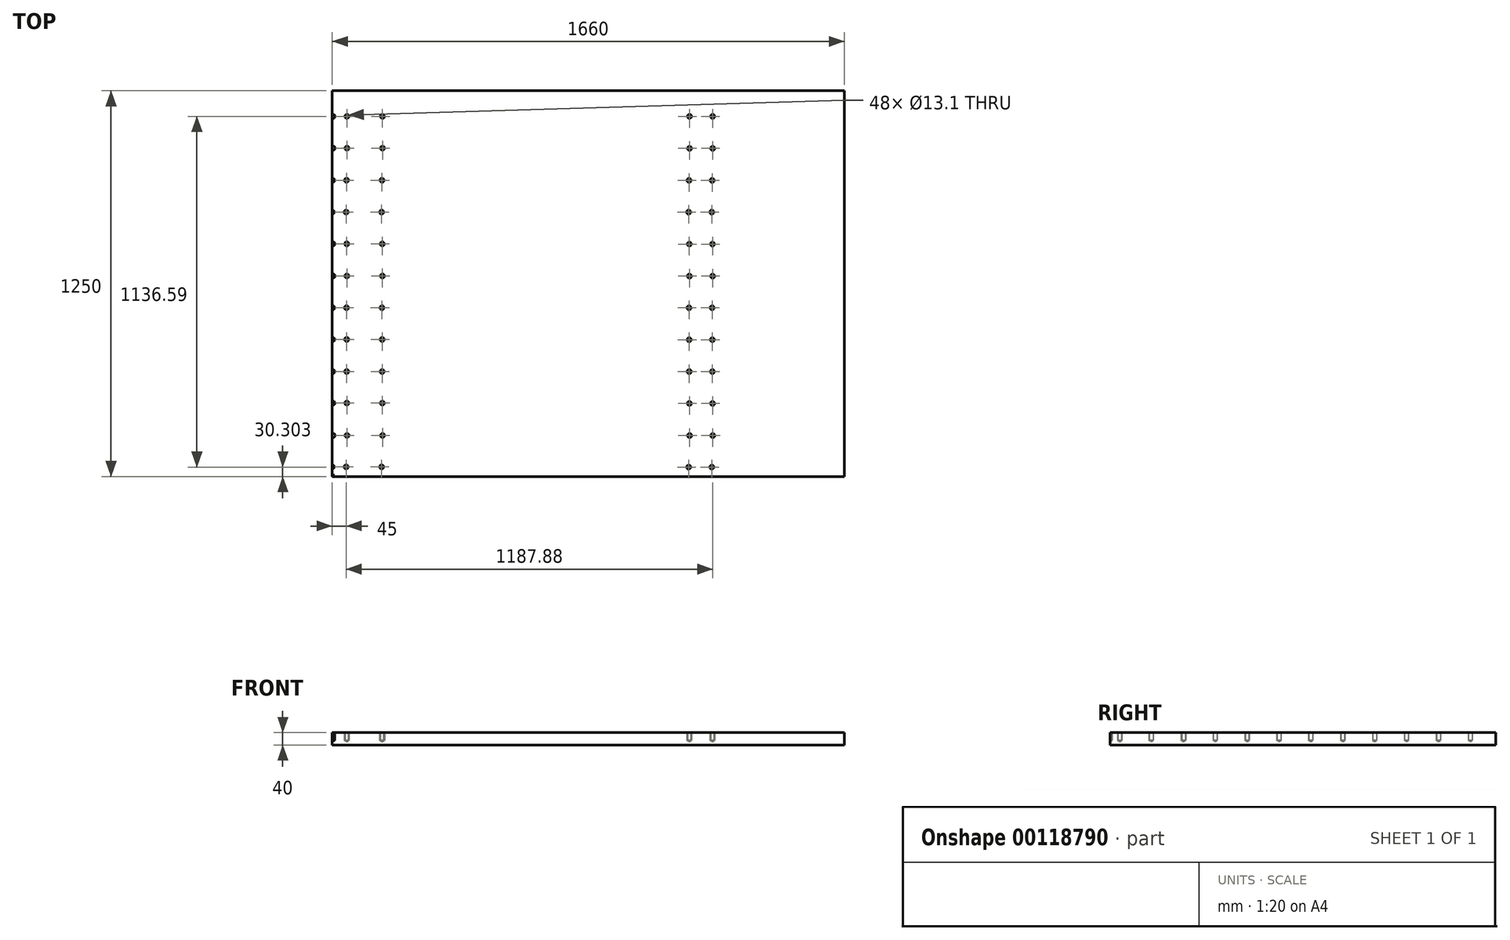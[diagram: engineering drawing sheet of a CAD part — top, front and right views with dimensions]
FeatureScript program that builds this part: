
annotation { "Feature Type Name" : "Feature", "Feature Type Description" : "" }
export const myFeature = defineFeature(function(context is Context, id is Id, definition is map)
    precondition{}
    {
        {
            var Q0;
            Q0=qCreatedBy(makeId("Top.planeOp"),FACE);
            var sketch = newSketch(context, id + "F0", { "sketchPlane" : qUnion([Q0])});
            skLineSegment(sketch, "E0", {"start": v(1662.59, 1166.8) * mm, "end": v(1232.59, 1166.82) * mm});
            skPoint(sketch, "E1", {"position": v(47.59, 1166.9) * mm});
            skPoint(sketch, "E2", {"position": v(162.59, 1166.89) * mm});
            skPoint(sketch, "E3", {"position": v(1157.59, 1166.83) * mm});
            skLineSegment(sketch, "E4", {"start": v(0, 0) * mm, "end": v(0, 0) * mm});
            skLineSegment(sketch, "E5", {"start": v(0, 0) * mm, "end": v(1660, 0) * mm});
            skLineSegment(sketch, "E6", {"start": v(1157.59, 1166.83) * mm, "end": v(162.59, 1166.89) * mm});
            skLineSegment(sketch, "E7", {"start": v(162.59, 1166.89) * mm, "end": v(47.59, 1166.9) * mm});
            skLineSegment(sketch, "E8", {"start": v(47.59, 1166.9) * mm, "end": v(2.59, 1166.9) * mm});
            skPoint(sketch, "E9", {"position": v(1232.59, 1166.82) * mm});
            skLineSegment(sketch, "E10", {"start": v(1232.59, 1166.82) * mm, "end": v(1157.59, 1166.83) * mm});
            skLineSegment(sketch, "E11.0.1.0", {"start": v(1157.75, 1063.3) * mm, "end": v(162.75, 1063.95) * mm});
            skPoint(sketch, "E11.0.1.1", {"position": v(1232.75, 1063.26) * mm});
            skPoint(sketch, "E11.0.1.2", {"position": v(162.75, 1063.95) * mm});
            skPoint(sketch, "E11.0.1.3", {"position": v(1157.75, 1063.3) * mm});
            skLineSegment(sketch, "E11.0.1.4", {"start": v(1232.75, 1063.26) * mm, "end": v(1157.75, 1063.3) * mm});
            skLineSegment(sketch, "E11.0.1.5", {"start": v(162.75, 1063.95) * mm, "end": v(47.75, 1064.02) * mm});
            skLineSegment(sketch, "E11.0.1.6", {"start": v(1662.75, 1062.99) * mm, "end": v(1232.75, 1063.26) * mm});
            skPoint(sketch, "E11.0.1.7", {"position": v(2.75, 1064.05) * mm});
            skLineSegment(sketch, "E11.0.1.8", {"start": v(47.75, 1064.02) * mm, "end": v(2.75, 1064.05) * mm});
            skLineSegment(sketch, "E11.0.2.0", {"start": v(1156.22, 959.51) * mm, "end": v(161.22, 959.88) * mm});
            skPoint(sketch, "E11.0.2.1", {"position": v(1231.22, 959.48) * mm});
            skPoint(sketch, "E11.0.2.2", {"position": v(46.22, 959.92) * mm});
            skPoint(sketch, "E11.0.2.3", {"position": v(1156.22, 959.51) * mm});
            skLineSegment(sketch, "E11.0.2.4", {"start": v(1231.22, 959.48) * mm, "end": v(1156.22, 959.51) * mm});
            skLineSegment(sketch, "E11.0.2.5", {"start": v(161.22, 959.88) * mm, "end": v(46.22, 959.92) * mm});
            skLineSegment(sketch, "E11.0.2.6", {"start": v(1661.22, 959.33) * mm, "end": v(1231.22, 959.48) * mm});
            skPoint(sketch, "E11.0.2.7", {"position": v(161.22, 959.88) * mm});
            skLineSegment(sketch, "E11.0.2.8", {"start": v(46.22, 959.92) * mm, "end": v(1.22, 959.94) * mm});
            skLineSegment(sketch, "E11.0.3.0", {"start": v(1155, 856.6) * mm, "end": v(160, 856.75) * mm});
            skPoint(sketch, "E11.0.3.1", {"position": v(1230, 856.59) * mm});
            skPoint(sketch, "E11.0.3.2", {"position": v(45, 856.76) * mm});
            skPoint(sketch, "E11.0.3.3", {"position": v(1155, 856.6) * mm});
            skLineSegment(sketch, "E11.0.3.4", {"start": v(1230, 856.59) * mm, "end": v(1155, 856.6) * mm});
            skLineSegment(sketch, "E11.0.3.5", {"start": v(160, 856.75) * mm, "end": v(45, 856.76) * mm});
            skLineSegment(sketch, "E11.0.3.6", {"start": v(1660, 856.53) * mm, "end": v(1230, 856.59) * mm});
            skPoint(sketch, "E11.0.3.7", {"position": v(160, 856.75) * mm});
            skLineSegment(sketch, "E11.0.3.8", {"start": v(45, 856.76) * mm, "end": v(0, 856.77) * mm});
            skLineSegment(sketch, "E11.0.4.0", {"start": v(1157.1, 753.1) * mm, "end": v(162.1, 753.67) * mm});
            skPoint(sketch, "E11.0.4.1", {"position": v(1232.1, 753.06) * mm});
            skPoint(sketch, "E11.0.4.2", {"position": v(47.1, 753.73) * mm});
            skPoint(sketch, "E11.0.4.3", {"position": v(1157.1, 753.1) * mm});
            skLineSegment(sketch, "E11.0.4.4", {"start": v(1232.1, 753.06) * mm, "end": v(1157.1, 753.1) * mm});
            skLineSegment(sketch, "E11.0.4.5", {"start": v(162.1, 753.67) * mm, "end": v(47.1, 753.73) * mm});
            skLineSegment(sketch, "E11.0.4.6", {"start": v(1662.1, 752.82) * mm, "end": v(1232.1, 753.06) * mm});
            skPoint(sketch, "E11.0.4.7", {"position": v(162.1, 753.67) * mm});
            skLineSegment(sketch, "E11.0.4.8", {"start": v(47.1, 753.73) * mm, "end": v(2.1, 753.76) * mm});
            skLineSegment(sketch, "E11.0.5.0", {"start": v(1157.5, 649.23) * mm, "end": v(162.5, 649.72) * mm});
            skPoint(sketch, "E11.0.5.1", {"position": v(1232.5, 649.19) * mm});
            skPoint(sketch, "E11.0.5.2", {"position": v(47.5, 649.78) * mm});
            skPoint(sketch, "E11.0.5.3", {"position": v(1157.5, 649.23) * mm});
            skLineSegment(sketch, "E11.0.5.4", {"start": v(1232.5, 649.19) * mm, "end": v(1157.5, 649.23) * mm});
            skLineSegment(sketch, "E11.0.5.5", {"start": v(162.5, 649.72) * mm, "end": v(47.5, 649.78) * mm});
            skLineSegment(sketch, "E11.0.5.6", {"start": v(1662.5, 648.98) * mm, "end": v(1232.5, 649.19) * mm});
            skPoint(sketch, "E11.0.5.7", {"position": v(162.5, 649.72) * mm});
            skLineSegment(sketch, "E11.0.5.8", {"start": v(47.5, 649.78) * mm, "end": v(2.5, 649.8) * mm});
            skLineSegment(sketch, "E11.0.6.0", {"start": v(1156.06, 546.54) * mm, "end": v(161.06, 546.75) * mm});
            skPoint(sketch, "E11.0.6.1", {"position": v(1231.06, 546.52) * mm});
            skPoint(sketch, "E11.0.6.2", {"position": v(46.06, 546.77) * mm});
            skPoint(sketch, "E11.0.6.3", {"position": v(1156.06, 546.54) * mm});
            skLineSegment(sketch, "E11.0.6.4", {"start": v(1231.06, 546.52) * mm, "end": v(1156.06, 546.54) * mm});
            skLineSegment(sketch, "E11.0.6.5", {"start": v(161.06, 546.75) * mm, "end": v(46.06, 546.77) * mm});
            skLineSegment(sketch, "E11.0.6.6", {"start": v(1661.06, 546.44) * mm, "end": v(1231.06, 546.52) * mm});
            skPoint(sketch, "E11.0.6.7", {"position": v(161.06, 546.75) * mm});
            skLineSegment(sketch, "E11.0.6.8", {"start": v(46.06, 546.77) * mm, "end": v(1.06, 546.78) * mm});
            skLineSegment(sketch, "E11.0.7.0", {"start": v(1156.68, 443.08) * mm, "end": v(161.68, 443.85) * mm});
            skPoint(sketch, "E11.0.7.1", {"position": v(1231.68, 443.03) * mm});
            skPoint(sketch, "E11.0.7.2", {"position": v(46.68, 443.94) * mm});
            skPoint(sketch, "E11.0.7.3", {"position": v(1156.68, 443.08) * mm});
            skLineSegment(sketch, "E11.0.7.4", {"start": v(1231.68, 443.03) * mm, "end": v(1156.68, 443.08) * mm});
            skLineSegment(sketch, "E11.0.7.5", {"start": v(161.68, 443.85) * mm, "end": v(46.68, 443.94) * mm});
            skLineSegment(sketch, "E11.0.7.6", {"start": v(1661.68, 442.7) * mm, "end": v(1231.68, 443.03) * mm});
            skPoint(sketch, "E11.0.7.7", {"position": v(161.68, 443.85) * mm});
            skLineSegment(sketch, "E11.0.7.8", {"start": v(46.68, 443.94) * mm, "end": v(1.68, 443.97) * mm});
            skLineSegment(sketch, "E11.0.8.0", {"start": v(1156.7, 339.77) * mm, "end": v(161.7, 339.9) * mm});
            skPoint(sketch, "E11.0.8.1", {"position": v(1231.7, 339.76) * mm});
            skPoint(sketch, "E11.0.8.2", {"position": v(46.7, 339.92) * mm});
            skPoint(sketch, "E11.0.8.3", {"position": v(1156.7, 339.77) * mm});
            skLineSegment(sketch, "E11.0.8.4", {"start": v(1231.7, 339.76) * mm, "end": v(1156.7, 339.77) * mm});
            skLineSegment(sketch, "E11.0.8.5", {"start": v(161.7, 339.9) * mm, "end": v(46.7, 339.92) * mm});
            skLineSegment(sketch, "E11.0.8.6", {"start": v(1661.7, 339.7) * mm, "end": v(1231.7, 339.76) * mm});
            skPoint(sketch, "E11.0.8.7", {"position": v(161.7, 339.9) * mm});
            skLineSegment(sketch, "E11.0.8.8", {"start": v(46.7, 339.92) * mm, "end": v(1.7, 339.93) * mm});
            skLineSegment(sketch, "E11.0.9.0", {"start": v(1157.29, 236.51) * mm, "end": v(162.29, 237.6) * mm});
            skPoint(sketch, "E11.0.9.1", {"position": v(1232.29, 236.43) * mm});
            skPoint(sketch, "E11.0.9.2", {"position": v(47.29, 237.73) * mm});
            skPoint(sketch, "E11.0.9.3", {"position": v(1157.29, 236.51) * mm});
            skLineSegment(sketch, "E11.0.9.4", {"start": v(1232.29, 236.43) * mm, "end": v(1157.29, 236.51) * mm});
            skLineSegment(sketch, "E11.0.9.5", {"start": v(162.29, 237.6) * mm, "end": v(47.29, 237.73) * mm});
            skLineSegment(sketch, "E11.0.9.6", {"start": v(1662.29, 235.96) * mm, "end": v(1232.29, 236.43) * mm});
            skPoint(sketch, "E11.0.9.7", {"position": v(162.29, 237.6) * mm});
            skLineSegment(sketch, "E11.0.9.8", {"start": v(47.29, 237.73) * mm, "end": v(2.29, 237.78) * mm});
            skLineSegment(sketch, "E11.0.10.0", {"start": v(1157.88, 132.54) * mm, "end": v(162.88, 132.88) * mm});
            skPoint(sketch, "E11.0.10.1", {"position": v(1232.88, 132.51) * mm});
            skPoint(sketch, "E11.0.10.2", {"position": v(47.88, 132.92) * mm});
            skPoint(sketch, "E11.0.10.3", {"position": v(1157.88, 132.54) * mm});
            skLineSegment(sketch, "E11.0.10.4", {"start": v(1232.88, 132.51) * mm, "end": v(1157.88, 132.54) * mm});
            skLineSegment(sketch, "E11.0.10.5", {"start": v(162.88, 132.88) * mm, "end": v(47.88, 132.92) * mm});
            skLineSegment(sketch, "E11.0.10.6", {"start": v(1662.88, 132.37) * mm, "end": v(1232.88, 132.51) * mm});
            skPoint(sketch, "E11.0.10.7", {"position": v(162.88, 132.88) * mm});
            skLineSegment(sketch, "E11.0.10.8", {"start": v(47.88, 132.92) * mm, "end": v(2.88, 132.94) * mm});
            skLineSegment(sketch, "E11.0.11.0", {"start": v(1155, 30.35) * mm, "end": v(160, 30.97) * mm});
            skPoint(sketch, "E11.0.11.1", {"position": v(1230, 30.3) * mm});
            skPoint(sketch, "E11.0.11.2", {"position": v(45, 31.04) * mm});
            skPoint(sketch, "E11.0.11.3", {"position": v(1155, 30.35) * mm});
            skLineSegment(sketch, "E11.0.11.4", {"start": v(1230, 30.3) * mm, "end": v(1155, 30.35) * mm});
            skLineSegment(sketch, "E11.0.11.5", {"start": v(160, 30.97) * mm, "end": v(45, 31.04) * mm});
            skLineSegment(sketch, "E11.0.11.6", {"start": v(1660, 30.04) * mm, "end": v(1230, 30.3) * mm});
            skPoint(sketch, "E11.0.11.7", {"position": v(160, 30.97) * mm});
            skLineSegment(sketch, "E11.0.11.8", {"start": v(45, 31.04) * mm, "end": v(0, 31.07) * mm});
            skLineSegment(sketch, "E11.direction1", {"start": v(2.59, 1166.9) * mm, "end": v(319.84, 1166.9) * mm, "construction": true});
            skPoint(sketch, "E12", {"position": v(47.75, 1064.02) * mm});
            skLineSegment(sketch, "E13", {"start": v(0, 0) * mm, "end": v(0, 1250) * mm});
            skLineSegment(sketch, "E14", {"start": v(0, 1250) * mm, "end": v(1660, 1250) * mm});
            skLineSegment(sketch, "E15", {"start": v(1660, 1250) * mm, "end": v(1660, 0) * mm});
            skSolve(sketch);
        }
        {
            var Q0;
            {var subQ4=sQuery(id+"F0.wireOp",EDGE,"E5");Q0=makeQuery(id+"F0.imprint","IMPRINT",FACE,{"disambiguationData":[TD([[makeQuery(id+"F0.imprint","IMPRINT",EDGE,{"derivedFrom":subQ4}),1.0]])]});}
            extrude(context, id + "F1", {"entities" : qUnion([Q0]), "oppositeDirection" : true, "depth" : 40 * mm, "offsetDistance" : 25 * mm});
        }
        {
            var Q0;
            Q0=sQuery(id+"F0.wireOp",VERTEX,"E11.0.11.3");
            var Q1;
            Q1=sQuery(id+"F0.wireOp",VERTEX,"E11.0.1.2");
            var Q2;
            Q2=sQuery(id+"F0.wireOp",VERTEX,"E11.0.5.2");
            var Q3;
            Q3=sQuery(id+"F0.wireOp",VERTEX,"E11.0.9.2");
            var Q4;
            Q4=sQuery(id+"F0.wireOp",VERTEX,"E11.0.6.1");
            var Q5;
            Q5=sQuery(id+"F0.wireOp",VERTEX,"E11.0.10.1");
            var Q6;
            Q6=sQuery(id+"F0.wireOp",VERTEX,"E11.0.5.1");
            var Q7;
            Q7=sQuery(id+"F0.wireOp",VERTEX,"E11.0.3.2");
            var Q8;
            Q8=sQuery(id+"F0.wireOp",VERTEX,"E11.0.2.1");
            var Q9;
            Q9=sQuery(id+"F0.wireOp",VERTEX,"E11.0.7.2");
            var Q10;
            Q10=sQuery(id+"F0.wireOp",VERTEX,"E11.0.9.1");
            var Q11;
            Q11=sQuery(id+"F0.wireOp",VERTEX,"E11.0.11.2");
            var Q12;
            Q12=sQuery(id+"F0.wireOp",VERTEX,"E11.0.5.7");
            var Q13;
            Q13=sQuery(id+"F0.wireOp",VERTEX,"E11.0.9.7");
            var Q14;
            Q14=sQuery(id+"F0.wireOp",VERTEX,"E11.0.1.1");
            var Q15;
            Q15=sQuery(id+"F0.wireOp",VERTEX,"E11.0.2.3");
            var Q16;
            Q16=sQuery(id+"F0.wireOp",VERTEX,"E11.0.4.1");
            var Q17;
            Q17=sQuery(id+"F0.wireOp",VERTEX,"E11.0.8.1");
            var Q18;
            Q18=sQuery(id+"F0.wireOp",VERTEX,"E12");
            var Q19;
            Q19=sQuery(id+"F0.wireOp",VERTEX,"E11.0.6.3");
            var Q20;
            Q20=sQuery(id+"F0.wireOp",VERTEX,"E11.0.10.3");
            var Q21;
            Q21=sQuery(id+"F0.wireOp",VERTEX,"E1");
            var Q22;
            Q22=sQuery(id+"F0.wireOp",VERTEX,"E11.0.1.3");
            var Q23;
            Q23=sQuery(id+"F0.wireOp",VERTEX,"E11.0.9.3");
            var Q24;
            Q24=sQuery(id+"F0.wireOp",VERTEX,"E11.0.5.3");
            var Q25;
            Q25=sQuery(id+"F0.wireOp",VERTEX,"E11.0.3.7");
            var Q26;
            Q26=sQuery(id+"F0.wireOp",VERTEX,"E11.0.11.7");
            var Q27;
            Q27=sQuery(id+"F0.wireOp",VERTEX,"E11.0.7.7");
            var Q28;
            Q28=sQuery(id+"F0.wireOp",VERTEX,"E11.0.3.1");
            var Q29;
            Q29=sQuery(id+"F0.wireOp",VERTEX,"E11.0.8.7");
            var Q30;
            Q30=sQuery(id+"F0.wireOp",VERTEX,"E11.0.4.7");
            var Q31;
            Q31=sQuery(id+"F0.wireOp",VERTEX,"E11.0.11.1");
            var Q32;
            Q32=sQuery(id+"F0.wireOp",VERTEX,"E11.0.7.1");
            var Q33;
            Q33=sQuery(id+"F0.wireOp",VERTEX,"E9");
            var Q34;
            Q34=sQuery(id+"F0.wireOp",VERTEX,"E11.0.6.2");
            var Q35;
            Q35=sQuery(id+"F0.wireOp",VERTEX,"E11.0.10.2");
            var Q36;
            Q36=sQuery(id+"F0.wireOp",VERTEX,"E11.0.2.2");
            var Q37;
            Q37=sQuery(id+"F0.wireOp",VERTEX,"E11.0.2.7");
            var Q38;
            Q38=sQuery(id+"F0.wireOp",VERTEX,"E11.0.6.7");
            var Q39;
            Q39=sQuery(id+"F0.wireOp",VERTEX,"E11.0.4.3");
            var Q40;
            Q40=sQuery(id+"F0.wireOp",VERTEX,"E11.0.8.3");
            var Q41;
            Q41=sQuery(id+"F0.wireOp",VERTEX,"E11.0.10.7");
            var Q42;
            Q42=sQuery(id+"F0.wireOp",VERTEX,"E3");
            var Q43;
            Q43=sQuery(id+"F0.wireOp",VERTEX,"E11.0.3.3");
            var Q44;
            Q44=sQuery(id+"F0.wireOp",VERTEX,"E11.0.7.3");
            var Q45;
            Q45=sQuery(id+"F0.wireOp",VERTEX,"E11.0.4.2");
            var Q46;
            Q46=sQuery(id+"F0.wireOp",VERTEX,"E11.0.8.2");
            var Q47;
            Q47=sQuery(id+"F0.wireOp",VERTEX,"E2");
            var Q48;
            Q48=sQuery(id+"F0.wireOp",VERTEX,"E8.end");
            var Q49;
            Q49=sQuery(id+"F0.wireOp",VERTEX,"E5.start");
            var Q50;
            Q50=sQuery(id+"F0.wireOp",VERTEX,"E11.0.11.8.end");
            var Q51;
            Q51=sQuery(id+"F0.wireOp",VERTEX,"E11.0.1.7");
            var Q52;
            Q52=sQuery(id+"F0.wireOp",VERTEX,"E11.0.10.8.end");
            var Q53;
            Q53=sQuery(id+"F0.wireOp",VERTEX,"E11.0.2.8.end");
            var Q54;
            Q54=sQuery(id+"F0.wireOp",VERTEX,"E11.0.3.8.end");
            var Q55;
            Q55=sQuery(id+"F0.wireOp",VERTEX,"E11.0.7.8.end");
            var Q56;
            Q56=sQuery(id+"F0.wireOp",VERTEX,"E11.0.6.8.end");
            var Q57;
            Q57=sQuery(id+"F0.wireOp",VERTEX,"E11.0.8.8.end");
            var Q58;
            Q58=sQuery(id+"F0.wireOp",VERTEX,"E11.0.9.8.end");
            var Q59;
            Q59=sQuery(id+"F0.wireOp",VERTEX,"E11.0.5.8.end");
            var Q60;
            Q60=sQuery(id+"F0.wireOp",VERTEX,"E11.0.4.8.end");
            var Q61;
            Q61=makeQuery(id+"F1.opExtrude","SWEPT_BODY",BODY,{"disambiguationData":[OSD([sQuery(id+"F0.wireOp",EDGE,"E5"),sQuery(id+"F0.wireOp",EDGE,"E13"),sQuery(id+"F0.wireOp",EDGE,"E14"),sQuery(id+"F0.wireOp",EDGE,"E15")])]});
            hole(context, id + "F2", {"style" : HoleStyle.SIMPLE, "endStyle" : HoleEndStyle.BLIND, "holeDiameter" : 13.1 * mm, "holeDepth" : 25 * mm, "tappedDepth" : 12 * mm, "tapClearance" : 3, "locations" : qUnion([Q0, Q1, Q2, Q3, Q4, Q5, Q6, Q7, Q8, Q9, Q10, Q11, Q12, Q13, Q14, Q15, Q16, Q17, Q18, Q19, Q20, Q21, Q22, Q23, Q24, Q25, Q26, Q27, Q28, Q29, Q30, Q31, Q32, Q33, Q34, Q35, Q36, Q37, Q38, Q39, Q40, Q41, Q42, Q43, Q44, Q45, Q46, Q47, Q48, Q49, Q50, Q51, Q52, Q53, Q54, Q55, Q56, Q57, Q58, Q59, Q60]), "scope" : qUnion([Q61]), "startStyle" : HoleStartStyle.SKETCH});
        }
    });
